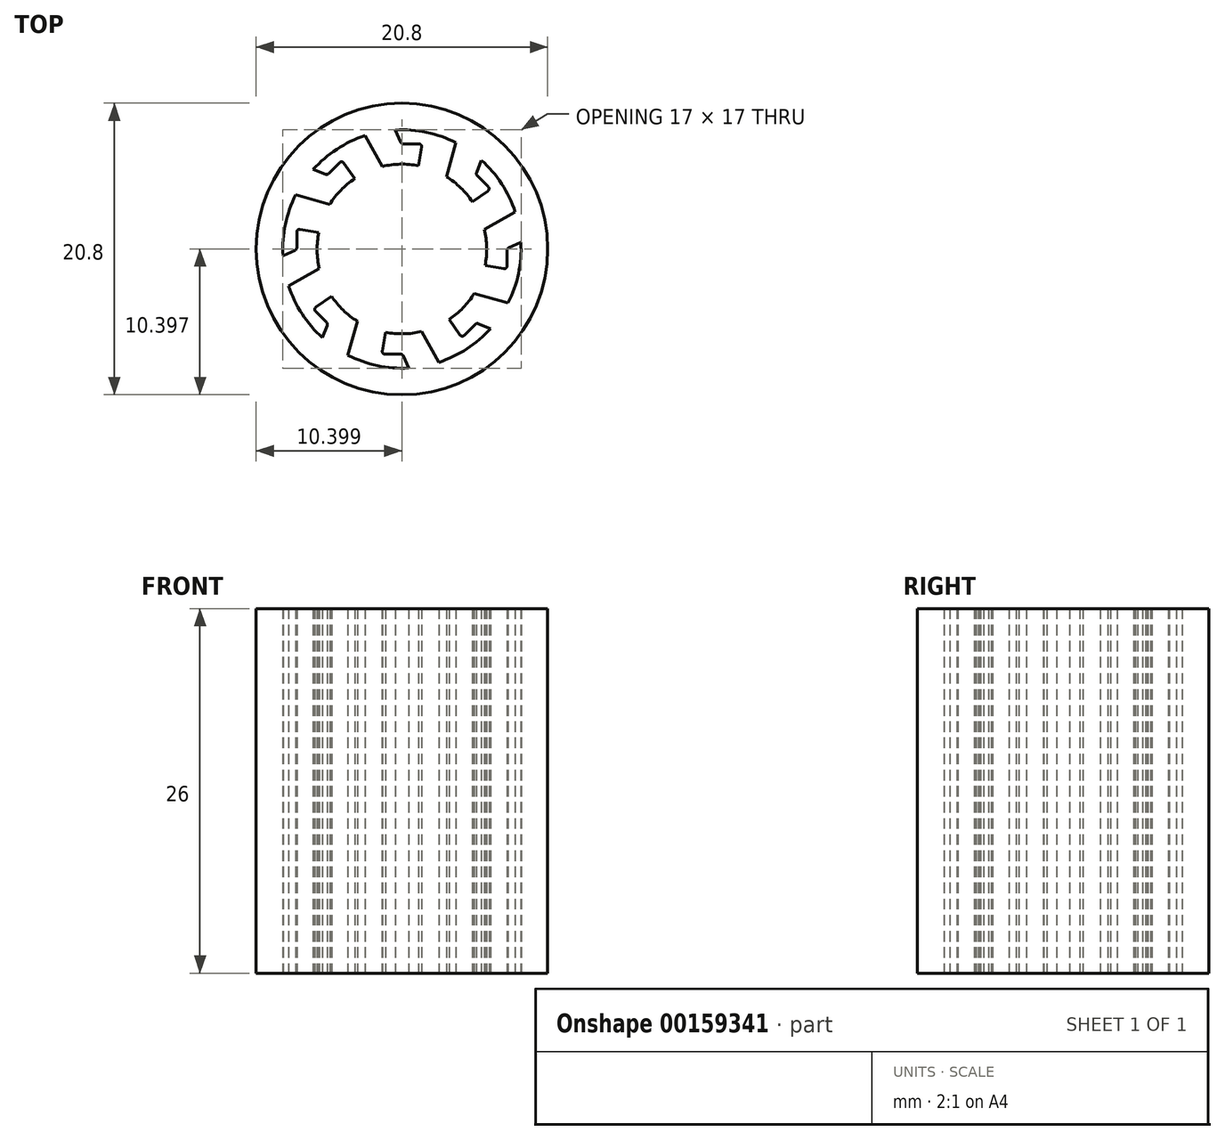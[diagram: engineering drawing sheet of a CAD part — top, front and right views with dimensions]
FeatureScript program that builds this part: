
annotation { "Feature Type Name" : "Feature", "Feature Type Description" : "" }
export const myFeature = defineFeature(function(context is Context, id is Id, definition is map)
    precondition{}
    {
        {
            var Q0;
            Q0=qCreatedBy(makeId("Top.planeOp"),FACE);
            var sketch = newSketch(context, id + "F0", { "sketchPlane" : qUnion([Q0])});
            skCircle(sketch, "E0", {"center": v(-0.02, -0.5) * mm, "radius": 6.05 * mm});
            skCircle(sketch, "E1", {"center": v(-0.02, -0.5) * mm, "radius": 10.4 * mm});
            skCircle(sketch, "E2", {"center": v(-0.02, -0.5) * mm, "radius": 8.5 * mm});
            skLineSegment(sketch, "E3", {"start": v(-2.65, 7.6) * mm, "end": v(-1.37, 5.3) * mm});
            skLineSegment(sketch, "E4", {"start": v(-1.37, 5.3) * mm, "end": v(1.13, 5.3) * mm});
            skLineSegment(sketch, "E5", {"start": v(1.13, 5.3) * mm, "end": v(1.39, 6.77) * mm});
            skLineSegment(sketch, "E6", {"start": v(1.19, 7) * mm, "end": v(0.08, 7) * mm});
            skLineSegment(sketch, "E7", {"start": v(-0.1, 7.13) * mm, "end": v(-0.49, 8) * mm});
            skPoint(sketch, "E8.visualSharp", {"position": v(1.43, 7) * mm});
            skArc(sketch, "E8.filletArc", {"start": v(1.39, 6.77) * mm, "mid": v(1.34, 6.93) * mm, "end": v(1.19, 7) * mm});
            skPoint(sketch, "E9.visualSharp", {"position": v(-0.05, 7) * mm});
            skArc(sketch, "E9.filletArc", {"start": v(-0.1, 7.13) * mm, "mid": v(-0.03, 7.04) * mm, "end": v(0.08, 7) * mm});
            skLineSegment(sketch, "E10.1.0", {"start": v(-5.08, 2.65) * mm, "end": v(-3.3, 4.42) * mm});
            skLineSegment(sketch, "E10.1.1", {"start": v(-7.6, 3.36) * mm, "end": v(-5.08, 2.65) * mm});
            skLineSegment(sketch, "E10.1.2", {"start": v(-5.47, 4.84) * mm, "end": v(-6.35, 5.18) * mm});
            skArc(sketch, "E10.1.3", {"start": v(-5.47, 4.84) * mm, "mid": v(-5.36, 4.83) * mm, "end": v(-5.25, 4.88) * mm});
            skLineSegment(sketch, "E10.1.4", {"start": v(-4.47, 5.66) * mm, "end": v(-5.25, 4.88) * mm});
            skArc(sketch, "E10.1.5", {"start": v(-4.16, 5.64) * mm, "mid": v(-4.3, 5.72) * mm, "end": v(-4.47, 5.66) * mm});
            skLineSegment(sketch, "E10.1.6", {"start": v(-3.3, 4.42) * mm, "end": v(-4.16, 5.64) * mm});
            skLineSegment(sketch, "E10.2.0", {"start": v(-5.82, -1.84) * mm, "end": v(-5.82, 0.66) * mm});
            skLineSegment(sketch, "E10.2.1", {"start": v(-8.1, -3.12) * mm, "end": v(-5.82, -1.84) * mm});
            skLineSegment(sketch, "E10.2.2", {"start": v(-7.64, -0.58) * mm, "end": v(-8.5, -0.96) * mm});
            skArc(sketch, "E10.2.3", {"start": v(-7.64, -0.58) * mm, "mid": v(-7.55, -0.5) * mm, "end": v(-7.52, -0.4) * mm});
            skLineSegment(sketch, "E10.2.4", {"start": v(-7.52, 0.71) * mm, "end": v(-7.52, -0.4) * mm});
            skArc(sketch, "E10.2.5", {"start": v(-7.28, 0.91) * mm, "mid": v(-7.45, 0.87) * mm, "end": v(-7.52, 0.71) * mm});
            skLineSegment(sketch, "E10.2.6", {"start": v(-5.82, 0.66) * mm, "end": v(-7.28, 0.91) * mm});
            skLineSegment(sketch, "E11.1.3.0", {"start": v(-3.17, -5.55) * mm, "end": v(-4.93, -3.78) * mm});
            skLineSegment(sketch, "E11.3.3.0", {"start": v(-3.88, -8.07) * mm, "end": v(-3.17, -5.55) * mm});
            skLineSegment(sketch, "E11.6.3.0", {"start": v(-5.35, -5.94) * mm, "end": v(-5.7, -6.82) * mm});
            skArc(sketch, "E11.9.3.0", {"start": v(-5.35, -5.94) * mm, "mid": v(-5.34, -5.83) * mm, "end": v(-5.4, -5.73) * mm});
            skLineSegment(sketch, "E11.13.3.0", {"start": v(-6.18, -4.94) * mm, "end": v(-5.4, -5.73) * mm});
            skArc(sketch, "E11.16.3.0", {"start": v(-6.15, -4.63) * mm, "mid": v(-6.24, -4.78) * mm, "end": v(-6.18, -4.94) * mm});
            skLineSegment(sketch, "E11.20.3.0", {"start": v(-4.93, -3.78) * mm, "end": v(-6.15, -4.63) * mm});
            skLineSegment(sketch, "E11.1.4.0", {"start": v(1.33, -6.3) * mm, "end": v(-1.17, -6.3) * mm});
            skLineSegment(sketch, "E11.3.4.0", {"start": v(2.6, -8.58) * mm, "end": v(1.33, -6.3) * mm});
            skLineSegment(sketch, "E11.6.4.0", {"start": v(0.07, -8.11) * mm, "end": v(0.45, -8.98) * mm});
            skArc(sketch, "E11.9.4.0", {"start": v(0.07, -8.11) * mm, "mid": v(0, -8.03) * mm, "end": v(-0.12, -8) * mm});
            skLineSegment(sketch, "E11.13.4.0", {"start": v(-1.23, -8) * mm, "end": v(-0.12, -8) * mm});
            skArc(sketch, "E11.16.4.0", {"start": v(-1.43, -7.75) * mm, "mid": v(-1.38, -7.92) * mm, "end": v(-1.23, -8) * mm});
            skLineSegment(sketch, "E11.20.4.0", {"start": v(-1.17, -6.3) * mm, "end": v(-1.43, -7.75) * mm});
            skLineSegment(sketch, "E11.1.5.0", {"start": v(5.04, -3.64) * mm, "end": v(3.27, -5.4) * mm});
            skLineSegment(sketch, "E11.3.5.0", {"start": v(7.55, -4.35) * mm, "end": v(5.04, -3.64) * mm});
            skLineSegment(sketch, "E11.6.5.0", {"start": v(5.43, -5.82) * mm, "end": v(6.31, -6.16) * mm});
            skArc(sketch, "E11.9.5.0", {"start": v(5.43, -5.82) * mm, "mid": v(5.31, -5.81) * mm, "end": v(5.21, -5.87) * mm});
            skLineSegment(sketch, "E11.13.5.0", {"start": v(4.43, -6.65) * mm, "end": v(5.21, -5.87) * mm});
            skArc(sketch, "E11.16.5.0", {"start": v(4.12, -6.62) * mm, "mid": v(4.27, -6.7) * mm, "end": v(4.43, -6.65) * mm});
            skLineSegment(sketch, "E11.20.5.0", {"start": v(3.27, -5.4) * mm, "end": v(4.12, -6.62) * mm});
            skLineSegment(sketch, "E12.1.6.0", {"start": v(5.78, 0.86) * mm, "end": v(5.78, -1.64) * mm});
            skLineSegment(sketch, "E12.3.6.0", {"start": v(8.06, 2.14) * mm, "end": v(5.78, 0.86) * mm});
            skLineSegment(sketch, "E12.6.6.0", {"start": v(7.6, -0.4) * mm, "end": v(8.47, -0.03) * mm});
            skArc(sketch, "E12.9.6.0", {"start": v(7.6, -0.4) * mm, "mid": v(7.51, -0.48) * mm, "end": v(7.48, -0.6) * mm});
            skLineSegment(sketch, "E12.13.6.0", {"start": v(7.48, -1.7) * mm, "end": v(7.48, -0.6) * mm});
            skArc(sketch, "E12.16.6.0", {"start": v(7.24, -1.9) * mm, "mid": v(7.4, -1.85) * mm, "end": v(7.48, -1.7) * mm});
            skLineSegment(sketch, "E12.20.6.0", {"start": v(5.78, -1.64) * mm, "end": v(7.24, -1.9) * mm});
            skLineSegment(sketch, "E12.1.7.0", {"start": v(3.12, 4.56) * mm, "end": v(4.9, 2.8) * mm});
            skLineSegment(sketch, "E12.3.7.0", {"start": v(3.84, 7.08) * mm, "end": v(3.12, 4.56) * mm});
            skLineSegment(sketch, "E12.6.7.0", {"start": v(5.3, 4.96) * mm, "end": v(5.65, 5.84) * mm});
            skArc(sketch, "E12.9.7.0", {"start": v(5.3, 4.96) * mm, "mid": v(5.3, 4.84) * mm, "end": v(5.35, 4.74) * mm});
            skLineSegment(sketch, "E12.13.7.0", {"start": v(6.14, 3.96) * mm, "end": v(5.35, 4.74) * mm});
            skArc(sketch, "E12.16.7.0", {"start": v(6.1, 3.65) * mm, "mid": v(6.2, 3.8) * mm, "end": v(6.14, 3.96) * mm});
            skLineSegment(sketch, "E12.20.7.0", {"start": v(4.9, 2.8) * mm, "end": v(6.1, 3.65) * mm});
            skSolve(sketch);
        }
        {
            var Q0;
            Q0 = qSketchRegion(id + "F0", true);
            var Q1;
            {var subQ0=sQuery(id+"F0.wireOp",EDGE,"E10.2.2");Q1=makeQuery(id+"F0.imprint","IMPRINT",FACE,{"disambiguationData":[TD([[makeQuery(id+"F0.imprint","IMPRINT",EDGE,{"derivedFrom":subQ0}),1.0]])]});}
            var Q2;
            {var subQ0=sQuery(id+"F0.wireOp",EDGE,"E10.1.2");Q2=makeQuery(id+"F0.imprint","IMPRINT",FACE,{"disambiguationData":[TD([[makeQuery(id+"F0.imprint","IMPRINT",EDGE,{"derivedFrom":subQ0}),1.0]])]});}
            var Q3;
            Q3=makeQuery(id+"F0.imprint","IMPRINT",FACE,{"disambiguationData":[TD([[makeQuery(id+"F0.imprint","IMPRINT",EDGE,{"derivedFrom":sQuery(id+"F0.wireOp",EDGE,"E6")}),1.0]])]});
            var Q4;
            {var subQ8=sQuery(id+"F0.wireOp",EDGE,"E12.6.7.0");Q4=makeQuery(id+"F0.imprint","IMPRINT",FACE,{"disambiguationData":[TD([[makeQuery(id+"F0.imprint","IMPRINT",EDGE,{"derivedFrom":subQ8}),1.0]])]});}
            var Q5;
            {var subQ3=sQuery(id+"F0.wireOp",EDGE,"E12.6.6.0");Q5=makeQuery(id+"F0.imprint","IMPRINT",FACE,{"disambiguationData":[TD([[makeQuery(id+"F0.imprint","IMPRINT",EDGE,{"derivedFrom":subQ3}),1.0]])]});}
            var Q6;
            {var subQ0=sQuery(id+"F0.wireOp",EDGE,"E11.6.5.0");Q6=makeQuery(id+"F0.imprint","IMPRINT",FACE,{"disambiguationData":[TD([[makeQuery(id+"F0.imprint","IMPRINT",EDGE,{"derivedFrom":subQ0}),1.0]])]});}
            var Q7;
            {var subQ5=sQuery(id+"F0.wireOp",EDGE,"E11.6.4.0");Q7=makeQuery(id+"F0.imprint","IMPRINT",FACE,{"disambiguationData":[TD([[makeQuery(id+"F0.imprint","IMPRINT",EDGE,{"derivedFrom":subQ5}),1.0]])]});}
            var Q8;
            {var subQ0=sQuery(id+"F0.wireOp",EDGE,"E11.6.3.0");Q8=makeQuery(id+"F0.imprint","IMPRINT",FACE,{"disambiguationData":[TD([[makeQuery(id+"F0.imprint","IMPRINT",EDGE,{"derivedFrom":subQ0}),1.0]])]});}
            extrude(context, id + "F1", {"entities" : qUnion([Q0, Q1, Q2, Q3, Q4, Q5, Q6, Q7, Q8]), "depth" : 26 * mm});
        }
    });
